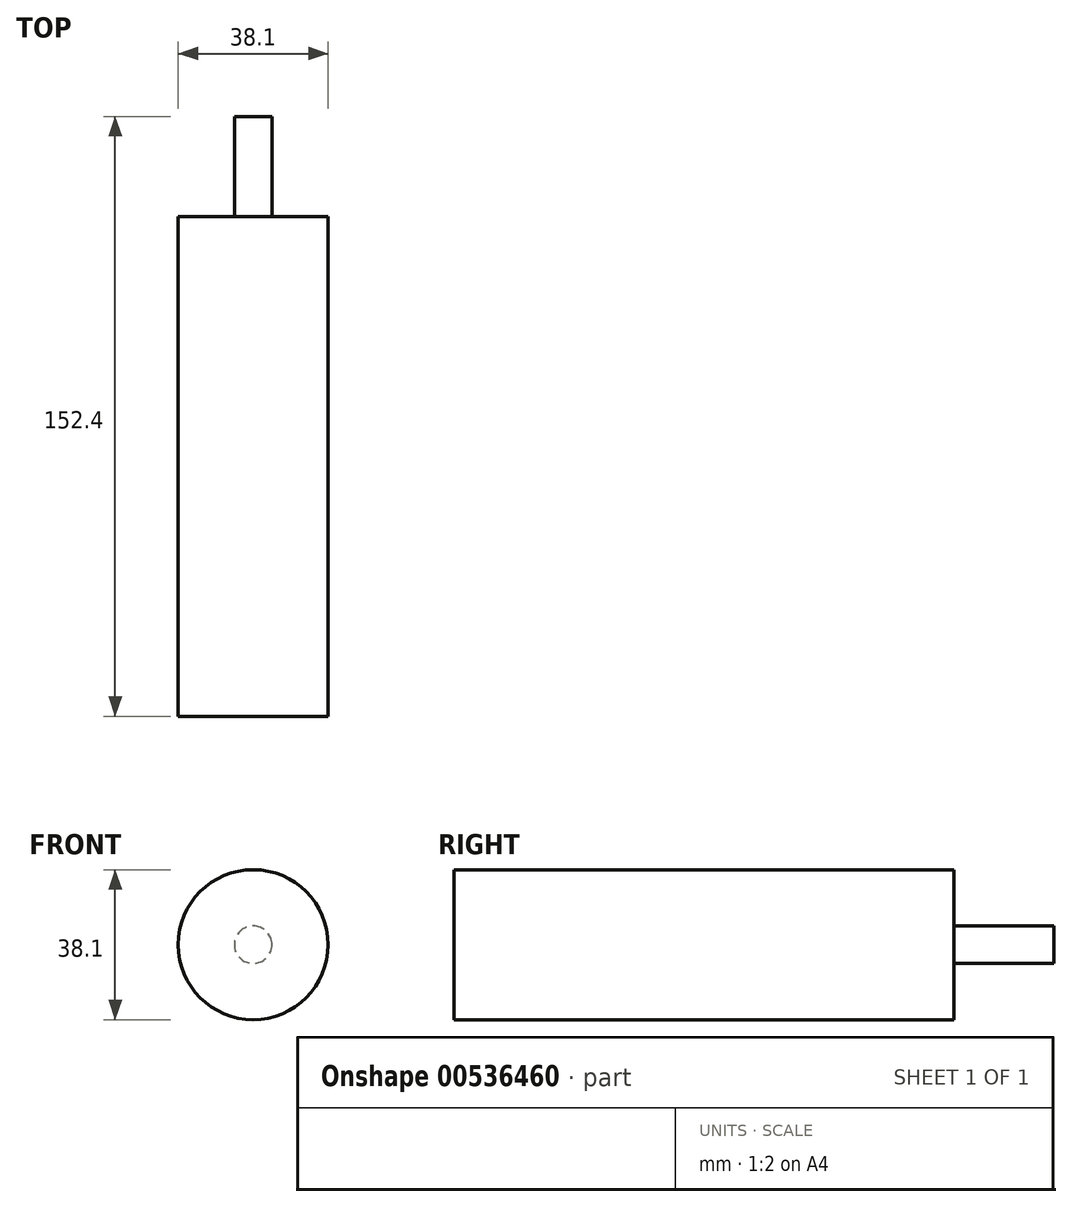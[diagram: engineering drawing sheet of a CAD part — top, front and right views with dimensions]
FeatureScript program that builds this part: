
annotation { "Feature Type Name" : "Feature", "Feature Type Description" : "" }
export const myFeature = defineFeature(function(context is Context, id is Id, definition is map)
    precondition{}
    {
        {
            var Q0;
            Q0=qCreatedBy(makeId("Front.planeOp"),FACE);
            var sketch = newSketch(context, id + "F0", { "sketchPlane" : qUnion([Q0])});
            skCircle(sketch, "E0", {"center": v(2.74, 7.53) * mm, "radius": 4.76 * mm});
            skSolve(sketch);
        }
        {
            var Q0;
            Q0=qSketchRegion(id+"F0",true);
            extrude(context, id + "F1", {"entities" : qUnion([Q0]), "depth" : 25.4 * mm, "offsetDistance" : 25.4 * mm});
        }
        {
            var Q0;
            Q0=makeQuery(id+"F1.opExtrude","CAP_FACE",FACE,{"disambiguationData":[OSD([sQuery(id+"F0.wireOp",EDGE,"E0")])],"isStart":false});
            var sketch = newSketch(context, id + "F2", { "sketchPlane" : qUnion([Q0])});
            skCircle(sketch, "E1", {"center": v(2.74, 7.53) * mm, "radius": 19.05 * mm});
            skSolve(sketch);
        }
        {
            var Q0;
            Q0 = qSketchRegion(id + "F2", true);
            extrude(context, id + "F3", {"entities" : qUnion([Q0]), "operationType" : NewBodyOperationType.ADD, "depth" : 127 * mm, "offsetDistance" : 25.4 * mm});
        }
    });
